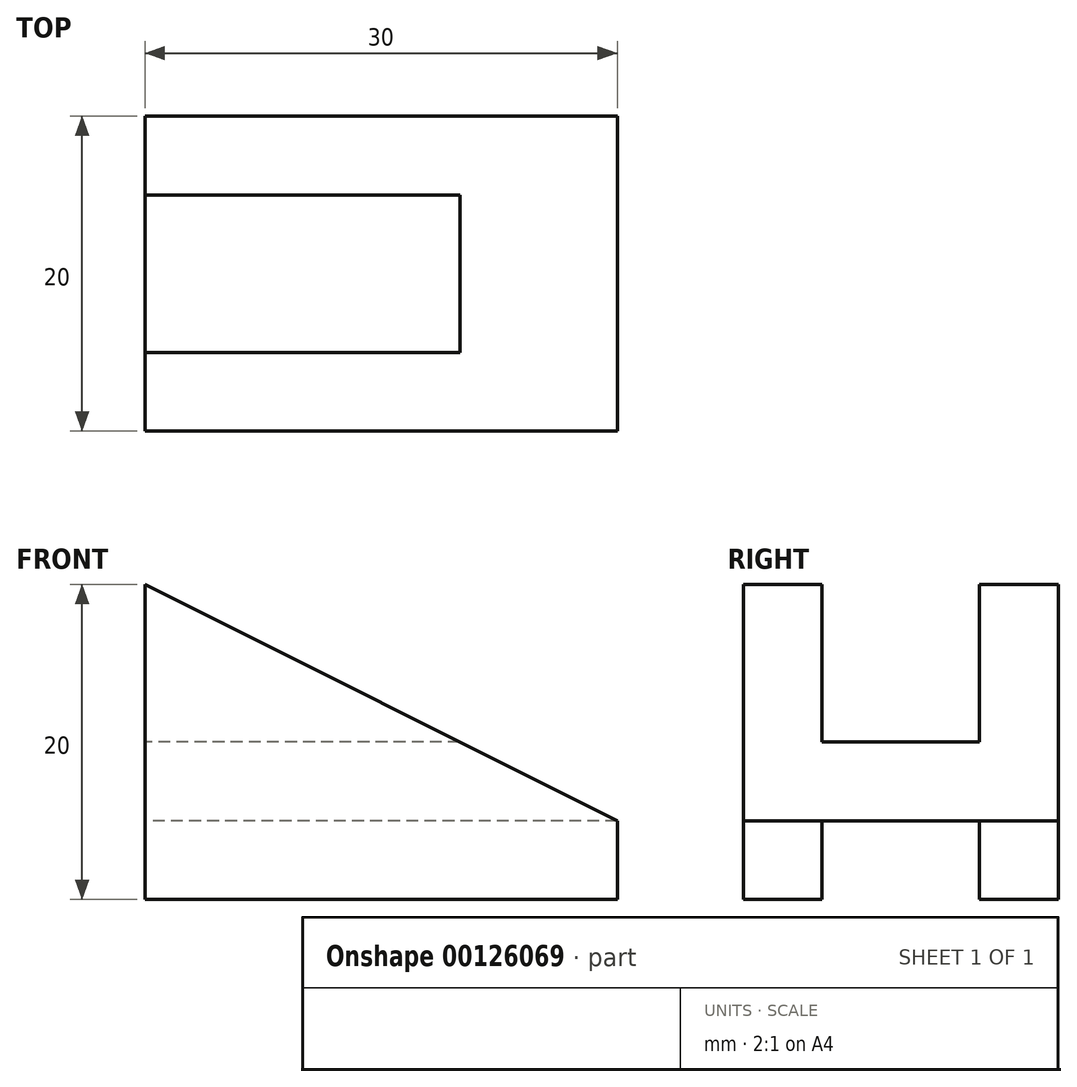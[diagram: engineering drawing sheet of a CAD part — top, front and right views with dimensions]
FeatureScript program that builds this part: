
annotation { "Feature Type Name" : "Feature", "Feature Type Description" : "" }
export const myFeature = defineFeature(function(context is Context, id is Id, definition is map)
    precondition{}
    {
        {
            var Q0;
            Q0=qCreatedBy(makeId("Front.planeOp"),FACE);
            var sketch = newSketch(context, id + "F0", { "sketchPlane" : qUnion([Q0])});
            skLineSegment(sketch, "E0.bottom", {"start": v(0, 0) * mm, "end": v(30, 0) * mm});
            skLineSegment(sketch, "E0.top", {"start": v(0, 20) * mm, "end": v(30, 20) * mm});
            skLineSegment(sketch, "E0.left", {"start": v(0, 0) * mm, "end": v(0, 20) * mm});
            skLineSegment(sketch, "E0.right", {"start": v(30, 0) * mm, "end": v(30, 20) * mm});
            skLineSegment(sketch, "E1", {"start": v(0, 20) * mm, "end": v(30, 5) * mm});
            skSolve(sketch);
        }
        {
            var Q0;
            {var subQ0=sQuery(id+"F0.wireOp",EDGE,"E0.bottom");Q0=makeQuery(id+"F0.imprint","IMPRINT",FACE,{"disambiguationData":[TD([[makeQuery(id+"F0.imprint","IMPRINT",EDGE,{"derivedFrom":subQ0}),1.0]])]});}
            extrude(context, id + "F1", {"entities" : qUnion([Q0]), "endBound" : BoundingType.SYMMETRIC, "depth" : 20 * mm});
        }
        {
            var Q0;
            Q0=makeQuery(id+"F1.opExtrude","SWEPT_FACE",FACE,{"disambiguationData":[OSD([sQuery(id+"F0.wireOp",EDGE,"E0.left")])]});
            var sketch = newSketch(context, id + "F2", { "sketchPlane" : qUnion([Q0])});
            skLineSegment(sketch, "E2.bottom", {"start": v(-5, 0) * mm, "end": v(5, 0) * mm});
            skLineSegment(sketch, "E2.top", {"start": v(-5, 5) * mm, "end": v(5, 5) * mm});
            skLineSegment(sketch, "E2.left", {"start": v(-5, 0) * mm, "end": v(-5, 5) * mm});
            skLineSegment(sketch, "E2.right", {"start": v(5, 0) * mm, "end": v(5, 5) * mm});
            skLineSegment(sketch, "E3.bottom", {"start": v(-5, 20) * mm, "end": v(5, 20) * mm});
            skLineSegment(sketch, "E3.top", {"start": v(-5, 10) * mm, "end": v(5, 10) * mm});
            skLineSegment(sketch, "E3.left", {"start": v(-5, 20) * mm, "end": v(-5, 10) * mm});
            skLineSegment(sketch, "E3.right", {"start": v(5, 20) * mm, "end": v(5, 10) * mm});
            skSolve(sketch);
        }
        {
            var Q0;
            Q0=makeQuery(id+"F2.imprint","IMPRINT",FACE,{"disambiguationData":[TD([[makeQuery(id+"F2.imprint","IMPRINT",EDGE,{"derivedFrom":sQuery(id+"F2.wireOp",EDGE,"E3.bottom")}),1.0]])]});
            var Q1;
            Q1=makeQuery(id+"F2.imprint","IMPRINT",FACE,{"disambiguationData":[TD([[makeQuery(id+"F2.imprint","IMPRINT",EDGE,{"derivedFrom":sQuery(id+"F2.wireOp",EDGE,"E2.bottom")}),-1.0]])]});
            extrude(context, id + "F3", {"entities" : qUnion([Q0, Q1]), "operationType" : NewBodyOperationType.REMOVE, "endBound" : BoundingType.THROUGH_ALL, "oppositeDirection" : true, "depth" : 25 * mm});
        }
    });
